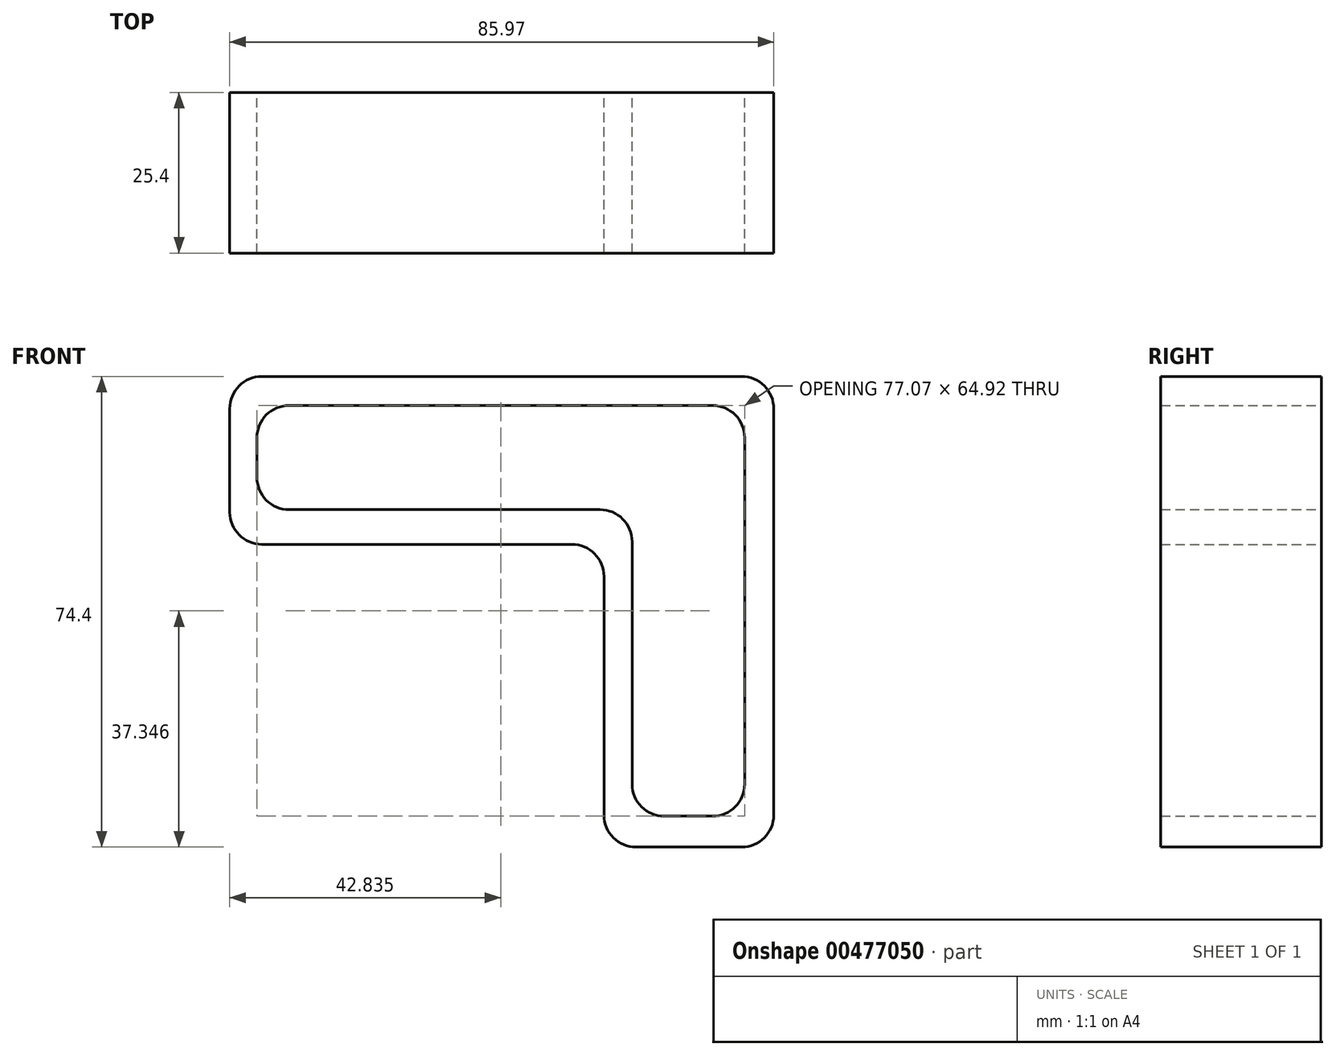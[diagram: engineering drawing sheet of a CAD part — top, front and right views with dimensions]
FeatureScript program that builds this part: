
annotation { "Feature Type Name" : "Feature", "Feature Type Description" : "" }
export const myFeature = defineFeature(function(context is Context, id is Id, definition is map)
    precondition{}
    {
        {
            var Q0;
            Q0=qCreatedBy(makeId("Front.planeOp"),FACE);
            var sketch = newSketch(context, id + "F0", { "sketchPlane" : qUnion([Q0])});
            skLineSegment(sketch, "E0.bottom", {"start": v(-44.2, 45.25) * mm, "end": v(32.87, 45.25) * mm});
            skLineSegment(sketch, "E0.top", {"start": v(-44.2, 28.8) * mm, "end": v(32.87, 28.8) * mm});
            skLineSegment(sketch, "E0.left", {"start": v(-44.2, 45.25) * mm, "end": v(-44.2, 28.8) * mm});
            skLineSegment(sketch, "E0.right", {"start": v(32.87, 45.25) * mm, "end": v(32.87, 28.8) * mm});
            skLineSegment(sketch, "E1.bottom", {"start": v(32.87, 28.8) * mm, "end": v(15.09, 28.8) * mm});
            skLineSegment(sketch, "E1.top", {"start": v(32.87, -19.67) * mm, "end": v(15.09, -19.67) * mm});
            skLineSegment(sketch, "E1.left", {"start": v(32.87, 28.8) * mm, "end": v(32.87, -19.67) * mm});
            skLineSegment(sketch, "E1.right", {"start": v(15.09, 28.8) * mm, "end": v(15.09, -19.67) * mm});
            skLineSegment(sketch, "E2.bottom", {"start": v(-48.5, 49.84) * mm, "end": v(37.47, 49.84) * mm});
            skLineSegment(sketch, "E2.top", {"start": v(-48.5, 23.3) * mm, "end": v(37.47, 23.3) * mm});
            skLineSegment(sketch, "E2.left", {"start": v(-48.5, 49.84) * mm, "end": v(-48.5, 23.3) * mm});
            skLineSegment(sketch, "E2.right", {"start": v(37.47, 49.84) * mm, "end": v(37.47, 23.3) * mm});
            skLineSegment(sketch, "E3.bottom", {"start": v(37.47, 23.3) * mm, "end": v(10.64, 23.3) * mm});
            skLineSegment(sketch, "E3.top", {"start": v(37.47, -24.56) * mm, "end": v(10.64, -24.56) * mm});
            skLineSegment(sketch, "E3.left", {"start": v(37.47, 23.3) * mm, "end": v(37.47, -24.56) * mm});
            skLineSegment(sketch, "E3.right", {"start": v(10.64, 23.3) * mm, "end": v(10.64, -24.56) * mm});
            skSolve(sketch);
        }
        {
            var Q0;
            Q0=makeQuery(id+"F0.imprint","IMPRINT",FACE,{"disambiguationData":[TD([[makeQuery(id+"F0.imprint","IMPRINT",EDGE,{"derivedFrom":sQuery(id+"F0.wireOp",EDGE,"E0.bottom")}),1.0]])]});
            var Q1;
            {var subQ5=sQuery(id+"F0.wireOp",EDGE,"E1.top");Q1=makeQuery(id+"F0.imprint","IMPRINT",FACE,{"disambiguationData":[TD([[makeQuery(id+"F0.imprint","IMPRINT",EDGE,{"derivedFrom":subQ5}),1.0]])]});}
            extrude(context, id + "F1", {"entities" : qUnion([Q0, Q1]), "depth" : 25.4 * mm});
        }
        {
            var Q0;
            Q0=makeQuery(id+"F1.opExtrude","SWEPT_EDGE",EDGE,{"disambiguationData":[OSD([sQuery(id+"F0.wireOp",EDGE,"E2.top"),sQuery(id+"F0.wireOp",EDGE,"E2.left")])]});
            var Q1;
            Q1=makeQuery(id+"F1.opExtrude","SWEPT_EDGE",EDGE,{"disambiguationData":[OSD([sQuery(id+"F0.wireOp",EDGE,"E2.top"),sQuery(id+"F0.wireOp",EDGE,"E3.bottom"),sQuery(id+"F0.wireOp",EDGE,"E3.right")])]});
            var Q2;
            Q2=makeQuery(id+"F1.opExtrude","SWEPT_EDGE",EDGE,{"disambiguationData":[OSD([sQuery(id+"F0.wireOp",EDGE,"E3.top"),sQuery(id+"F0.wireOp",EDGE,"E3.right")])]});
            var Q3;
            Q3=makeQuery(id+"F1.opExtrude","SWEPT_EDGE",EDGE,{"disambiguationData":[OSD([sQuery(id+"F0.wireOp",EDGE,"E3.top"),sQuery(id+"F0.wireOp",EDGE,"E3.left")])]});
            var Q4;
            Q4=makeQuery(id+"F1.opExtrude","SWEPT_EDGE",EDGE,{"disambiguationData":[OSD([sQuery(id+"F0.wireOp",EDGE,"E2.bottom"),sQuery(id+"F0.wireOp",EDGE,"E2.right")])]});
            var Q5;
            Q5=makeQuery(id+"F1.opExtrude","SWEPT_EDGE",EDGE,{"disambiguationData":[OSD([sQuery(id+"F0.wireOp",EDGE,"E2.bottom"),sQuery(id+"F0.wireOp",EDGE,"E2.left")])]});
            var Q6;
            Q6=makeQuery(id+"F1.opExtrude","SWEPT_EDGE",EDGE,{"disambiguationData":[OSD([sQuery(id+"F0.wireOp",EDGE,"E1.top"),sQuery(id+"F0.wireOp",EDGE,"E1.left")])]});
            var Q7;
            Q7=makeQuery(id+"F1.opExtrude","SWEPT_EDGE",EDGE,{"disambiguationData":[OSD([sQuery(id+"F0.wireOp",EDGE,"E0.top"),sQuery(id+"F0.wireOp",EDGE,"E1.bottom"),sQuery(id+"F0.wireOp",EDGE,"E1.right")])]});
            var Q8;
            Q8=makeQuery(id+"F1.opExtrude","SWEPT_EDGE",EDGE,{"disambiguationData":[OSD([sQuery(id+"F0.wireOp",EDGE,"E1.top"),sQuery(id+"F0.wireOp",EDGE,"E1.right")])]});
            var Q9;
            Q9=makeQuery(id+"F1.opExtrude","SWEPT_EDGE",EDGE,{"disambiguationData":[OSD([sQuery(id+"F0.wireOp",EDGE,"E0.bottom"),sQuery(id+"F0.wireOp",EDGE,"E0.left")])]});
            var Q10;
            Q10=makeQuery(id+"F1.opExtrude","SWEPT_EDGE",EDGE,{"disambiguationData":[OSD([sQuery(id+"F0.wireOp",EDGE,"E0.bottom"),sQuery(id+"F0.wireOp",EDGE,"E0.right")])]});
            var Q11;
            Q11=makeQuery(id+"F1.opExtrude","SWEPT_EDGE",EDGE,{"disambiguationData":[OSD([sQuery(id+"F0.wireOp",EDGE,"E0.top"),sQuery(id+"F0.wireOp",EDGE,"E0.left")])]});
            fillet(context, id + "F2", {"entities" : qUnion([Q0, Q1, Q2, Q3, Q4, Q5, Q6, Q7, Q8, Q9, Q10, Q11]), "radius" : 5.08 * mm, "tangentPropagation" : true, "allowEdgeOverflow" : false});
        }
    });
